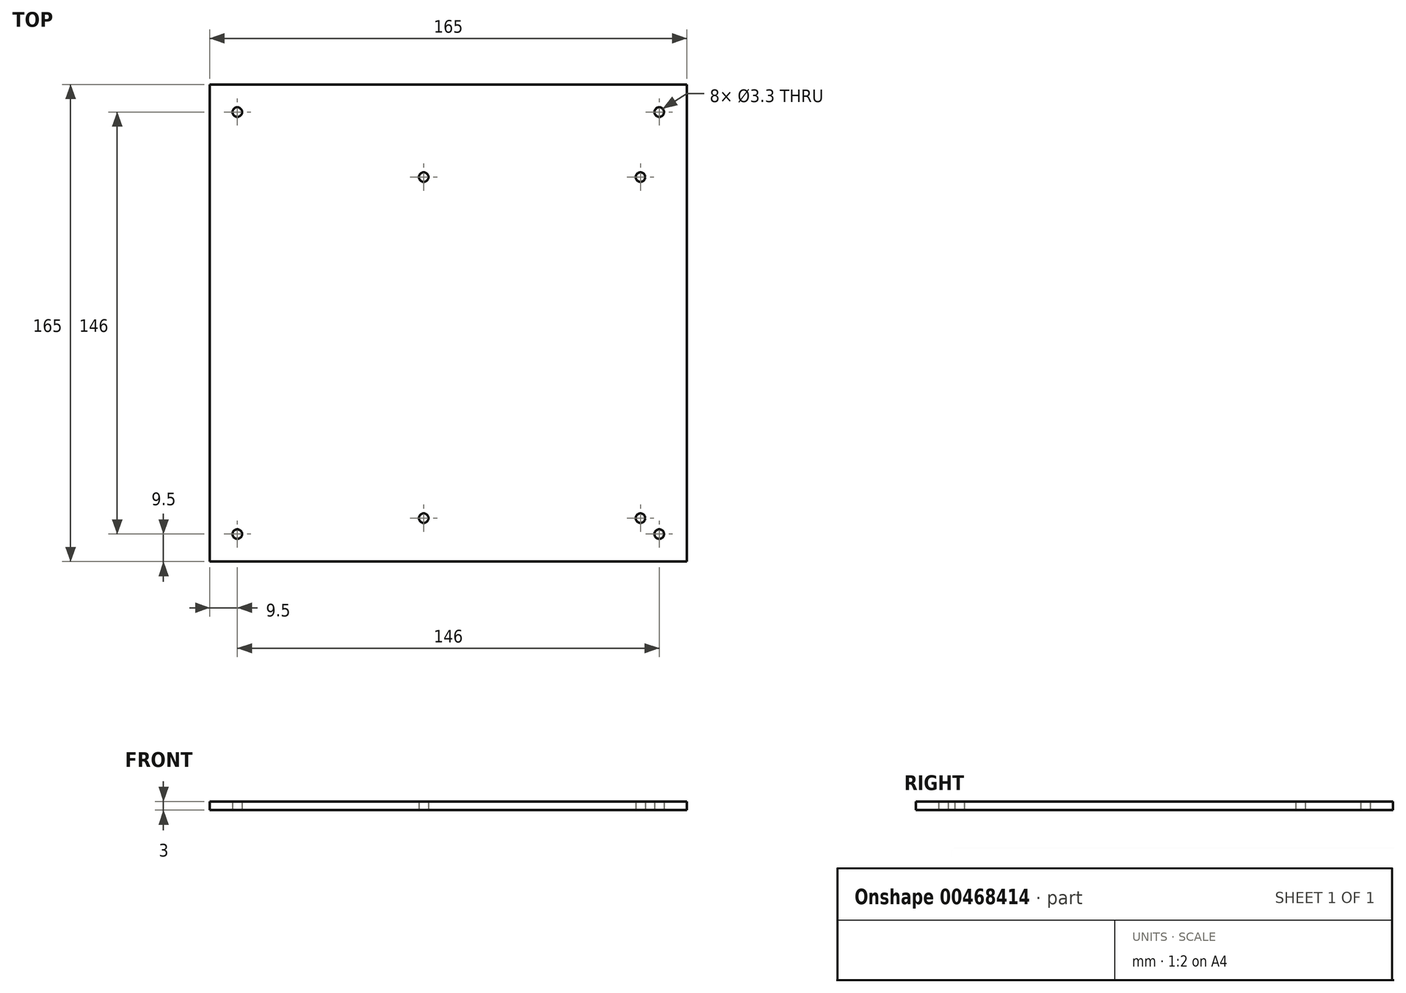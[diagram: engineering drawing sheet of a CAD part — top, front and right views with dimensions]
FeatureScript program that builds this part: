
annotation { "Feature Type Name" : "Feature", "Feature Type Description" : "" }
export const myFeature = defineFeature(function(context is Context, id is Id, definition is map)
    precondition{}
    {
        {
            var Q0;
            Q0=qCreatedBy(makeId("Top.planeOp"),FACE);
            var sketch = newSketch(context, id + "F0", { "sketchPlane" : qUnion([Q0])});
            skLineSegment(sketch, "E0.bottom", {"start": v(82.5, 82.5) * mm, "end": v(-82.5, 82.5) * mm});
            skLineSegment(sketch, "E0.top", {"start": v(82.5, -82.5) * mm, "end": v(-82.5, -82.5) * mm});
            skLineSegment(sketch, "E0.left", {"start": v(82.5, 82.5) * mm, "end": v(82.5, -82.5) * mm});
            skLineSegment(sketch, "E0.right", {"start": v(-82.5, 82.5) * mm, "end": v(-82.5, -82.5) * mm});
            skPoint(sketch, "E0.middle", {"position": v(0, 0) * mm});
            skLineSegment(sketch, "E1.bottom", {"start": v(-8.5, 50.5) * mm, "end": v(66.5, 50.5) * mm, "construction": true});
            skLineSegment(sketch, "E1.top", {"start": v(-8.5, -67.5) * mm, "end": v(66.5, -67.5) * mm, "construction": true});
            skLineSegment(sketch, "E1.left", {"start": v(-8.5, 50.5) * mm, "end": v(-8.5, -67.5) * mm, "construction": true});
            skLineSegment(sketch, "E1.right", {"start": v(66.5, 50.5) * mm, "end": v(66.5, -67.5) * mm, "construction": true});
            skLineSegment(sketch, "E2.bottom", {"start": v(73, 73) * mm, "end": v(-73, 73) * mm, "construction": true});
            skLineSegment(sketch, "E2.top", {"start": v(73, -73) * mm, "end": v(-73, -73) * mm, "construction": true});
            skLineSegment(sketch, "E2.left", {"start": v(73, 73) * mm, "end": v(73, -73) * mm, "construction": true});
            skLineSegment(sketch, "E2.right", {"start": v(-73, 73) * mm, "end": v(-73, -73) * mm, "construction": true});
            skSolve(sketch);
        }
        {
            var Q0;
            Q0=makeQuery(id+"F0.imprint","IMPRINT",FACE,{"disambiguationData":[TD([[makeQuery(id+"F0.imprint","IMPRINT",EDGE,{"derivedFrom":sQuery(id+"F0.wireOp",EDGE,"E0.bottom")}),1.0]])]});
            extrude(context, id + "F1", {"entities" : qUnion([Q0]), "depth" : 3 * mm});
        }
        {
            var Q0;
            Q0=sQuery(id+"F0.wireOp",VERTEX,"E2.bottom.end");
            var Q1;
            Q1=sQuery(id+"F0.wireOp",VERTEX,"E2.bottom.start");
            var Q2;
            Q2=sQuery(id+"F0.wireOp",VERTEX,"E1.left.start");
            var Q3;
            Q3=sQuery(id+"F0.wireOp",VERTEX,"E1.right.start");
            var Q4;
            Q4=sQuery(id+"F0.wireOp",VERTEX,"E1.right.end");
            var Q5;
            Q5=sQuery(id+"F0.wireOp",VERTEX,"E1.left.end");
            var Q6;
            Q6=sQuery(id+"F0.wireOp",VERTEX,"E2.top.start");
            var Q7;
            Q7=sQuery(id+"F0.wireOp",VERTEX,"E2.right.end");
            var Q8;
            Q8=makeQuery(id+"F1.opExtrude","SWEPT_BODY",BODY,{"disambiguationData":[OSD([sQuery(id+"F0.wireOp",EDGE,"E0.bottom"),sQuery(id+"F0.wireOp",EDGE,"E0.top"),sQuery(id+"F0.wireOp",EDGE,"E0.left"),sQuery(id+"F0.wireOp",EDGE,"E0.right")])]});
            hole(context, id + "F2", {"style" : HoleStyle.SIMPLE, "endStyle" : HoleEndStyle.BLIND, "oppositeDirection" : true, "standardTappedOrClearance" : lookupTablePath({ "standard" : "ISO", "fit" : "Normal", "size" : "M3", "type" : "Clearance" }), "standardBlindInLast" : lookupTablePath({ "fit" : "Standard", "standard" : "ISO", "size" : "M3", "type" : "Clearance" }), "holeDiameter" : 3.3 * mm, "holeDepth" : 15 * mm, "isTappedThrough" : true, "tappedDepth" : 12 * mm, "tapClearance" : 3, "startFromSketch" : true, "locations" : qUnion([Q0, Q1, Q2, Q3, Q4, Q5, Q6, Q7]), "scope" : qUnion([Q8])});
        }
    });
